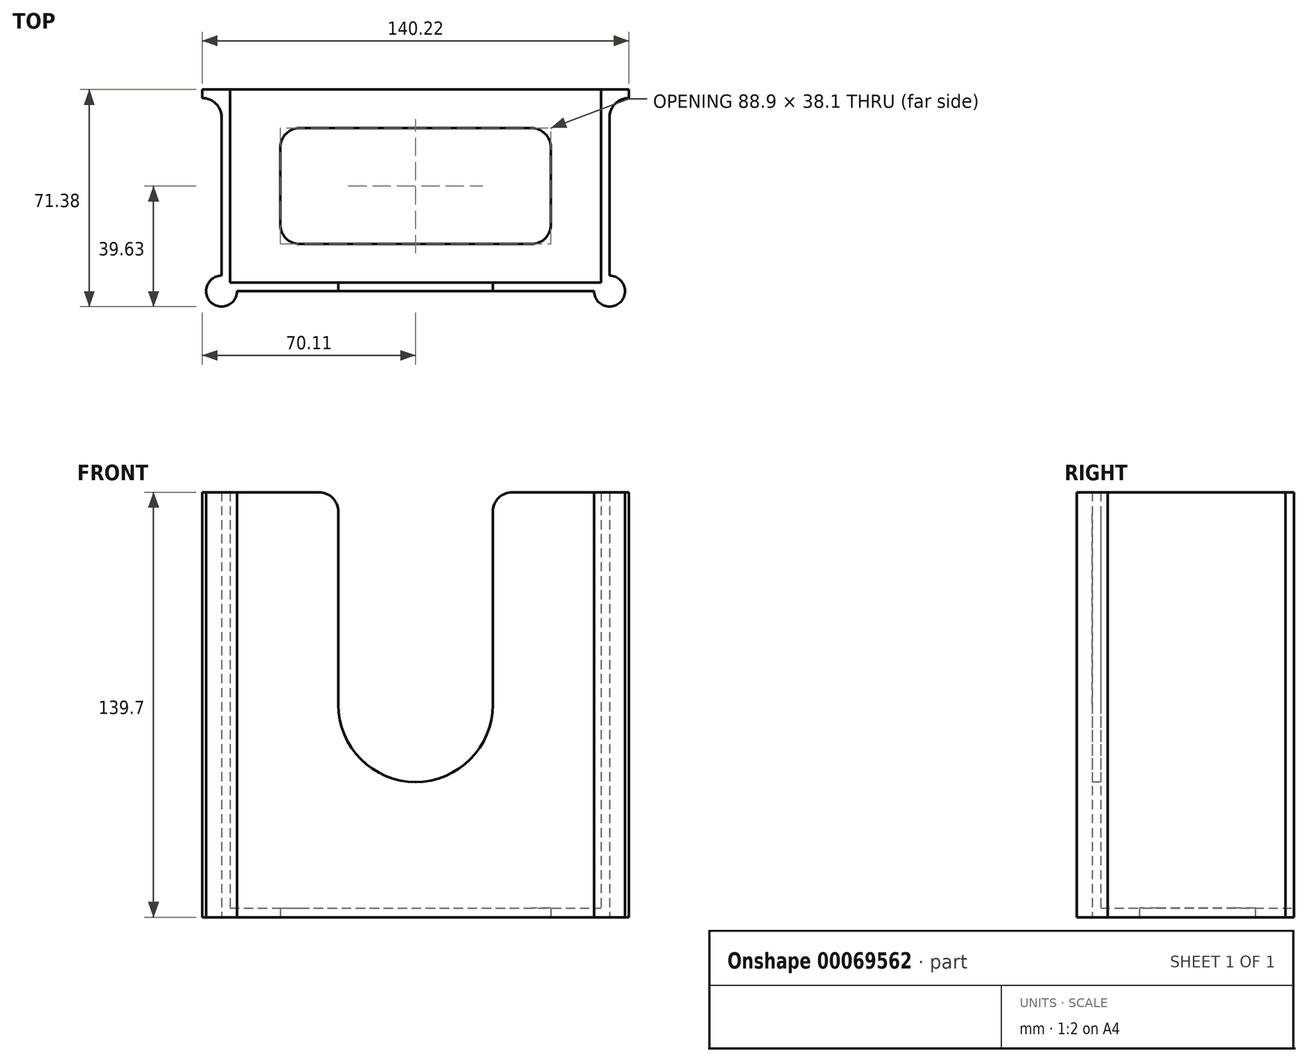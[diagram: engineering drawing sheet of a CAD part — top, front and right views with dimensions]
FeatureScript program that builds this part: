
annotation { "Feature Type Name" : "Feature", "Feature Type Description" : "" }
export const myFeature = defineFeature(function(context is Context, id is Id, definition is map)
    precondition{}
    {
        {
            var Q0;
            Q0=qCreatedBy(makeId("Top.planeOp"),FACE);
            var sketch = newSketch(context, id + "F0", { "sketchPlane" : qUnion([Q0])});
            skLineSegment(sketch, "E0", {"start": v(0, 0) * mm, "end": v(0, 63.5) * mm, "construction": true});
            skLineSegment(sketch, "E1", {"start": v(-60.96, 0) * mm, "end": v(60.96, 0) * mm});
            skLineSegment(sketch, "E2", {"start": v(60.96, 0) * mm, "end": v(60.96, 63.5) * mm});
            skLineSegment(sketch, "E3", {"start": v(60.96, 63.5) * mm, "end": v(70.11, 63.5) * mm});
            skLineSegment(sketch, "E4", {"start": v(-60.96, 0) * mm, "end": v(-60.96, 63.5) * mm});
            skLineSegment(sketch, "E5", {"start": v(-60.96, 63.5) * mm, "end": v(-70.11, 63.5) * mm});
            skLineSegment(sketch, "E6", {"start": v(-70.11, 63.5) * mm, "end": v(-70.11, 60.7) * mm});
            skLineSegment(sketch, "E7", {"start": v(-70.11, 60.7) * mm, "end": v(-70.11, 60.7) * mm});
            skLineSegment(sketch, "E8", {"start": v(-63.76, 54.35) * mm, "end": v(-63.76, -2.8) * mm});
            skLineSegment(sketch, "E9", {"start": v(-63.76, -2.8) * mm, "end": v(63.76, -2.8) * mm});
            skLineSegment(sketch, "E10", {"start": v(63.76, -2.8) * mm, "end": v(63.76, 54.35) * mm});
            skLineSegment(sketch, "E11", {"start": v(70.11, 60.7) * mm, "end": v(70.11, 60.7) * mm});
            skLineSegment(sketch, "E12", {"start": v(70.11, 60.7) * mm, "end": v(70.11, 63.5) * mm});
            skPoint(sketch, "E13.visualSharp", {"position": v(-63.76, 60.7) * mm});
            skArc(sketch, "E13.filletArc", {"start": v(-63.76, 54.35) * mm, "mid": v(-65.62, 58.84) * mm, "end": v(-70.11, 60.7) * mm});
            skPoint(sketch, "E14.visualSharp", {"position": v(63.76, 60.7) * mm});
            skArc(sketch, "E14.filletArc", {"start": v(70.11, 60.7) * mm, "mid": v(65.62, 58.84) * mm, "end": v(63.76, 54.35) * mm});
            skArc(sketch, "E15", {"start": v(-63.76, 2.28) * mm, "mid": v(-67.35, -6.4) * mm, "end": v(-58.68, -2.8) * mm});
            skArc(sketch, "E16", {"start": v(63.76, 2.28) * mm, "mid": v(67.35, -6.4) * mm, "end": v(58.68, -2.8) * mm});
            skSolve(sketch);
        }
        {
            var Q0;
            Q0 = qSketchRegion(id + "F0", true);
            extrude(context, id + "F1", {"entities" : qUnion([Q0]), "depth" : 139.7 * mm});
        }
        {
            var Q0;
            Q0=makeQuery(id+"F1.opExtrude","SWEPT_FACE",FACE,{"disambiguationData":[OSD([sQuery(id+"F0.wireOp",EDGE,"E9")])]});
            var sketch = newSketch(context, id + "F2", { "sketchPlane" : qUnion([Q0])});
            skArc(sketch, "E17", {"start": v(-25.4, 69.85) * mm, "mid": v(0, 44.45) * mm, "end": v(25.4, 69.85) * mm});
            skLineSegment(sketch, "E18", {"start": v(-25.4, 69.85) * mm, "end": v(-25.4, 133.35) * mm});
            skLineSegment(sketch, "E19", {"start": v(25.4, 69.85) * mm, "end": v(25.4, 133.35) * mm});
            skLineSegment(sketch, "E20", {"start": v(-31.75, 139.7) * mm, "end": v(-38.78, 139.7) * mm});
            skLineSegment(sketch, "E21", {"start": v(-38.78, 139.7) * mm, "end": v(-38.78, 151.02) * mm});
            skLineSegment(sketch, "E22", {"start": v(-38.78, 151.02) * mm, "end": v(41.9, 151.02) * mm});
            skLineSegment(sketch, "E23", {"start": v(41.9, 151.02) * mm, "end": v(41.9, 139.7) * mm});
            skLineSegment(sketch, "E24", {"start": v(41.9, 139.7) * mm, "end": v(31.75, 139.7) * mm});
            skPoint(sketch, "E25.visualSharp", {"position": v(25.4, 139.7) * mm});
            skArc(sketch, "E25.filletArc", {"start": v(31.75, 139.7) * mm, "mid": v(27.26, 137.84) * mm, "end": v(25.4, 133.35) * mm});
            skPoint(sketch, "E26.visualSharp", {"position": v(-25.4, 139.7) * mm});
            skArc(sketch, "E26.filletArc", {"start": v(-25.4, 133.35) * mm, "mid": v(-27.26, 137.84) * mm, "end": v(-31.75, 139.7) * mm});
            skSolve(sketch);
        }
        {
            var Q0;
            Q0 = qSketchRegion(id + "F2", true);
            extrude(context, id + "F3", {"entities" : qUnion([Q0]), "operationType" : NewBodyOperationType.REMOVE, "endBound" : BoundingType.THROUGH_ALL, "oppositeDirection" : true, "depth" : 25.4 * mm});
        }
        {
            var Q0;
            Q0=qCreatedBy(makeId("Top.planeOp"),FACE);
            var sketch = newSketch(context, id + "F4", { "sketchPlane" : qUnion([Q0])});
            skLineSegment(sketch, "E27.bottom", {"start": v(-63.3, 63.5) * mm, "end": v(62.7, 63.5) * mm});
            skLineSegment(sketch, "E27.top", {"start": v(-63.3, -1.82) * mm, "end": v(62.7, -1.82) * mm});
            skLineSegment(sketch, "E27.left", {"start": v(-63.3, 63.5) * mm, "end": v(-63.3, -1.82) * mm});
            skLineSegment(sketch, "E27.right", {"start": v(62.7, 63.5) * mm, "end": v(62.7, -1.82) * mm});
            skLineSegment(sketch, "E28.bottom", {"start": v(-38.1, 50.8) * mm, "end": v(38.1, 50.8) * mm});
            skLineSegment(sketch, "E28.top", {"start": v(-38.1, 12.7) * mm, "end": v(38.1, 12.7) * mm});
            skLineSegment(sketch, "E28.left", {"start": v(-44.45, 44.45) * mm, "end": v(-44.45, 19.05) * mm});
            skLineSegment(sketch, "E28.right", {"start": v(44.45, 44.45) * mm, "end": v(44.45, 19.05) * mm});
            skLineSegment(sketch, "E29", {"start": v(0, 0) * mm, "end": v(0, 63.5) * mm, "construction": true});
            skPoint(sketch, "E30.visualSharp", {"position": v(-44.45, 50.8) * mm});
            skArc(sketch, "E30.filletArc", {"start": v(-38.1, 50.8) * mm, "mid": v(-42.6, 48.94) * mm, "end": v(-44.45, 44.45) * mm});
            skPoint(sketch, "E31.visualSharp", {"position": v(-44.45, 12.7) * mm});
            skArc(sketch, "E31.filletArc", {"start": v(-44.45, 19.05) * mm, "mid": v(-42.6, 14.56) * mm, "end": v(-38.1, 12.7) * mm});
            skPoint(sketch, "E32.visualSharp", {"position": v(44.45, 12.7) * mm});
            skArc(sketch, "E32.filletArc", {"start": v(38.1, 12.7) * mm, "mid": v(42.6, 14.56) * mm, "end": v(44.45, 19.05) * mm});
            skPoint(sketch, "E33.visualSharp", {"position": v(44.45, 50.8) * mm});
            skArc(sketch, "E33.filletArc", {"start": v(44.45, 44.45) * mm, "mid": v(42.6, 48.94) * mm, "end": v(38.1, 50.8) * mm});
            skSolve(sketch);
        }
        {
            var Q0;
            Q0=makeQuery(id+"F4.imprint","IMPRINT",FACE,{"disambiguationData":[TD([[makeQuery(id+"F4.imprint","IMPRINT",EDGE,{"derivedFrom":sQuery(id+"F4.wireOp",EDGE,"E27.bottom")}),-1.0]])]});
            extrude(context, id + "F5", {"entities" : qUnion([Q0]), "operationType" : NewBodyOperationType.ADD, "depth" : 3 * mm});
        }
    });
